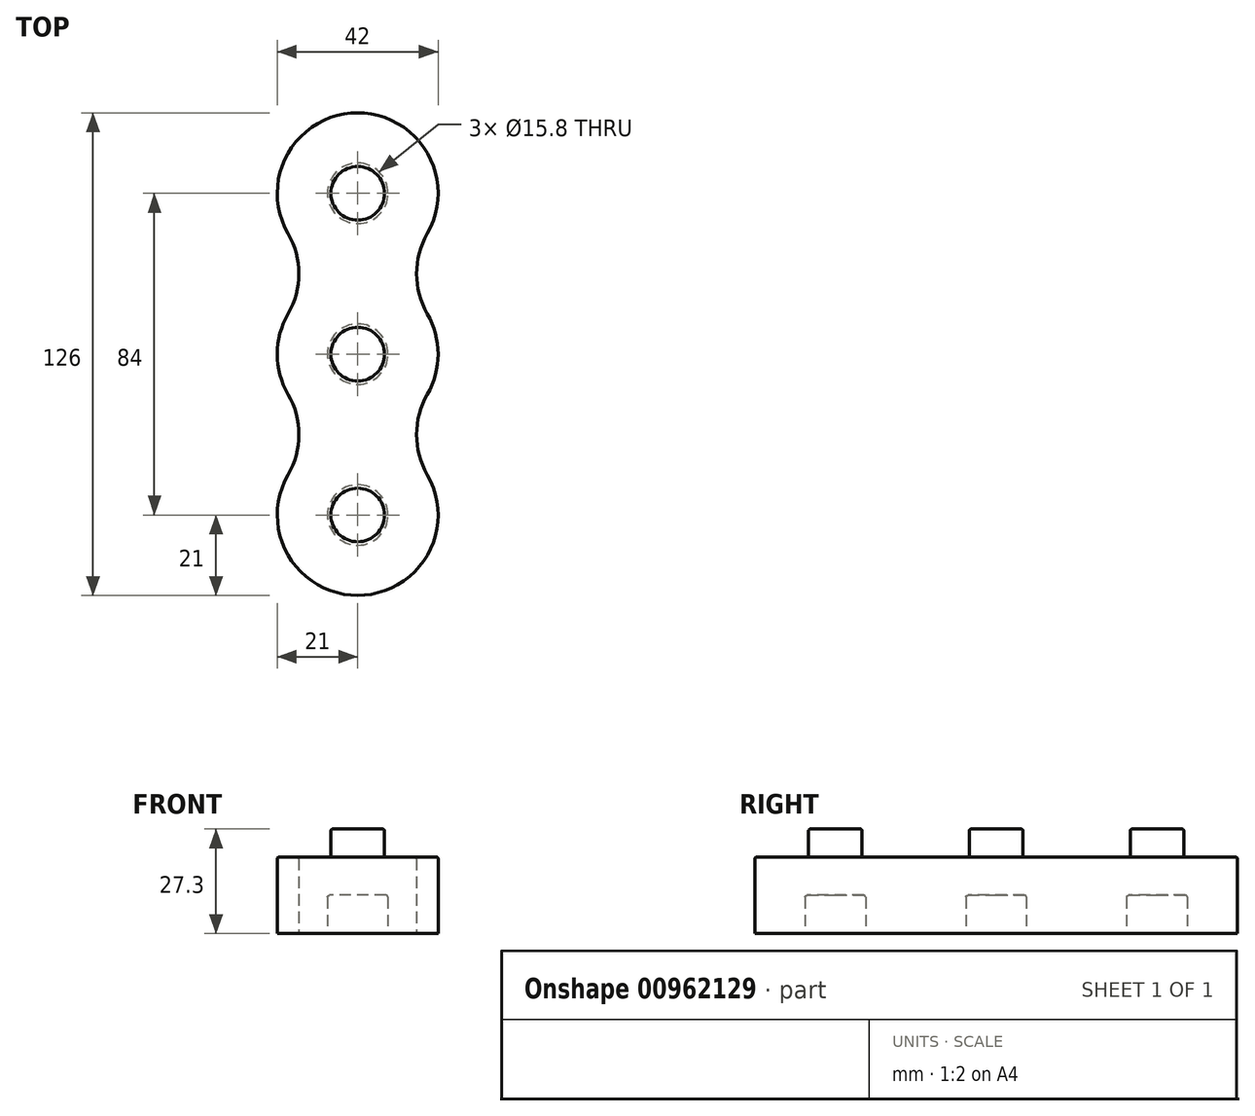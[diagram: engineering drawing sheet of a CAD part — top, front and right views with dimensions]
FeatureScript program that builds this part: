
annotation { "Feature Type Name" : "Feature", "Feature Type Description" : "" }
export const myFeature = defineFeature(function(context is Context, id is Id, definition is map)
    precondition{}
    {
        {
            assignVariable(context, id + "F0", {"name" : "inner_circle_extrude", "anyValue" : 10});
        }
        {
            assignVariable(context, id + "F1", {"name" : "nipple_circle_extrude", "anyValue" : 7.3});
        }
        {
            assignVariable(context, id + "F2", {"name" : "outer_circle_extrude", "anyValue" : 20});
        }
        {
            assignVariable(context, id + "F3", {"name" : "fillet", "anyValue" : 0.5});
        }
        {
            var Q0;
            Q0=qCreatedBy(makeId("Top.planeOp"),FACE);
            var sketch = newSketch(context, id + "F4", { "sketchPlane" : qUnion([Q0])});
            skCircle(sketch, "E0", {"center": v(0, 42) * mm, "radius": 7.9 * mm});
            skCircle(sketch, "E1", {"center": v(0, 0) * mm, "radius": 7.9 * mm});
            skArc(sketch, "E2.converted", {"start": v(18.19, 31.5) * mm, "mid": v(21, 42) * mm, "end": v(18.19, 52.5) * mm});
            skArc(sketch, "E3.converted", {"start": v(-18.19, 10.5) * mm, "mid": v(0, -21) * mm, "end": v(18.19, 10.5) * mm});
            skPoint(sketch, "E4.orphan", {"position": v(-18.87, 9.22) * mm});
            skArc(sketch, "E5", {"start": v(-18.19, 10.5) * mm, "mid": v(-15.37, 21) * mm, "end": v(-18.19, 31.5) * mm});
            skArc(sketch, "E6.MirrorC", {"start": v(18.19, 10.5) * mm, "mid": v(15.37, 21) * mm, "end": v(18.19, 31.5) * mm});
            skArc(sketch, "E7", {"start": v(18.19, 73.5) * mm, "mid": v(0, 105) * mm, "end": v(-18.19, 73.5) * mm});
            skArc(sketch, "E8", {"start": v(-18.19, 52.5) * mm, "mid": v(-15.37, 63) * mm, "end": v(-18.19, 73.5) * mm});
            skArc(sketch, "E9", {"start": v(18.19, 73.5) * mm, "mid": v(15.37, 63) * mm, "end": v(18.19, 52.5) * mm});
            skCircle(sketch, "E10", {"center": v(0, 84) * mm, "radius": 7.9 * mm});
            skArc(sketch, "E11.trimOffspring", {"start": v(-18.19, 52.5) * mm, "mid": v(-21, 42) * mm, "end": v(-18.19, 31.5) * mm});
            skSolve(sketch);
        }
        {
            var Q0;
            Q0=makeQuery(id+"F4.imprint","IMPRINT",FACE,{"disambiguationData":[TD([[makeQuery(id+"F4.imprint","IMPRINT",EDGE,{"derivedFrom":sQuery(id+"F4.wireOp",EDGE,"ScaTM9CG-l0WX-AUfX-dH3G-diZ5i2Zft3Bz")}),1.0]])]});
            var Q1;
            Q1=makeQuery(id+"F4.imprint","IMPRINT",FACE,{"disambiguationData":[TD([[makeQuery(id+"F4.imprint","IMPRINT",EDGE,{"derivedFrom":sQuery(id+"F4.wireOp",EDGE,"E0")}),1.0]])]});
            var Q2;
            Q2=makeQuery(id+"F4.imprint","IMPRINT",FACE,{"disambiguationData":[TD([[makeQuery(id+"F4.imprint","IMPRINT",EDGE,{"derivedFrom":sQuery(id+"F4.wireOp",EDGE,"E1")}),1.0]])]});
            var Q3;
            Q3=makeQuery(id+"F4.imprint","IMPRINT",FACE,{"disambiguationData":[TD([[makeQuery(id+"F4.imprint","IMPRINT",EDGE,{"derivedFrom":sQuery(id+"F4.wireOp",EDGE,"E0")}),-1.0]])]});
            var Q4;
            Q4=makeQuery(id+"F4.imprint","IMPRINT",FACE,{"disambiguationData":[TD([[makeQuery(id+"F4.imprint","IMPRINT",EDGE,{"derivedFrom":sQuery(id+"F4.wireOp",EDGE,"E10")}),1.0]])]});
            extrude(context, id + "F5", {"entities" : qUnion([Q0, Q1, Q2, Q3, Q4]), "depth" : (getVariable(context, 'outer_circle_extrude')) * mm, "offsetDistance" : 25 * mm});
        }
        {
            var Q0;
            Q0=makeQuery(id+"F4.imprint","IMPRINT",FACE,{"disambiguationData":[TD([[makeQuery(id+"F4.imprint","IMPRINT",EDGE,{"derivedFrom":sQuery(id+"F4.wireOp",EDGE,"E0")}),1.0]])]});
            var Q1;
            Q1=makeQuery(id+"F4.imprint","IMPRINT",FACE,{"disambiguationData":[TD([[makeQuery(id+"F4.imprint","IMPRINT",EDGE,{"derivedFrom":sQuery(id+"F4.wireOp",EDGE,"E1")}),1.0]])]});
            var Q2;
            Q2=makeQuery(id+"F4.imprint","IMPRINT",FACE,{"disambiguationData":[TD([[makeQuery(id+"F4.imprint","IMPRINT",EDGE,{"derivedFrom":sQuery(id+"F4.wireOp",EDGE,"E10")}),1.0]])]});
            extrude(context, id + "F6", {"entities" : qUnion([Q0, Q1, Q2]), "operationType" : NewBodyOperationType.REMOVE, "depth" : (getVariable(context, 'inner_circle_extrude')) * mm, "offsetDistance" : 25 * mm});
        }
        {
            var Q0;
            Q0=makeQuery(id+"F5.opExtrude","CAP_FACE",FACE,{"disambiguationData":[OSD([sQuery(id+"F4.wireOp",EDGE,"E2.converted"),sQuery(id+"F4.wireOp",EDGE,"E3.converted"),sQuery(id+"F4.wireOp",EDGE,"E5"),sQuery(id+"F4.wireOp",EDGE,"E6.MirrorC")])],"isStart":false});
            var sketch = newSketch(context, id + "F7", { "sketchPlane" : qUnion([Q0])});
            skCircle(sketch, "E12", {"center": v(0, 0) * mm, "radius": 7 * mm});
            skCircle(sketch, "E13", {"center": v(0, 42) * mm, "radius": 7 * mm});
            skCircle(sketch, "E14", {"center": v(0, 84) * mm, "radius": 7 * mm});
            skSolve(sketch);
        }
        {
            var Q0;
            Q0=makeQuery(id+"F7.imprint","IMPRINT",FACE,{"disambiguationData":[TD([[makeQuery(id+"F7.imprint","IMPRINT",EDGE,{"derivedFrom":sQuery(id+"F7.wireOp",EDGE,"E12")}),1.0]])]});
            var Q1;
            Q1=makeQuery(id+"F7.imprint","IMPRINT",FACE,{"disambiguationData":[TD([[makeQuery(id+"F7.imprint","IMPRINT",EDGE,{"derivedFrom":sQuery(id+"F7.wireOp",EDGE,"Dg55u7MG-Wcnn-qXMQ-j3jR-78wnB7IFwmOc")}),1.0]])]});
            var Q2;
            Q2=makeQuery(id+"F7.imprint","IMPRINT",FACE,{"disambiguationData":[TD([[makeQuery(id+"F7.imprint","IMPRINT",EDGE,{"derivedFrom":sQuery(id+"F7.wireOp",EDGE,"E13")}),1.0]])]});
            var Q3;
            Q3=makeQuery(id+"F7.imprint","IMPRINT",FACE,{"disambiguationData":[TD([[makeQuery(id+"F7.imprint","IMPRINT",EDGE,{"derivedFrom":sQuery(id+"F7.wireOp",EDGE,"E14")}),1.0]])]});
            extrude(context, id + "F8", {"entities" : qUnion([Q0, Q1, Q2, Q3]), "operationType" : NewBodyOperationType.ADD, "depth" : (getVariable(context, 'nipple_circle_extrude')) * mm, "offsetDistance" : 25 * mm});
        }
        {
            var Q0;
            Q0=makeQuery(id+"F8.opExtrude","CAP_EDGE",EDGE,{"disambiguationData":[OSD([sQuery(id+"F7.wireOp",EDGE,"E12")])],"isStart":false});
            var Q1;
            Q1=makeQuery(id+"F5.opExtrude","CAP_EDGE",EDGE,{"disambiguationData":[OSD([sQuery(id+"F4.wireOp",EDGE,"ScaTM9CG-l0WX-AUfX-dH3G-diZ5i2Zft3Bz")])],"isStart":false});
            var Q2;
            Q2=makeQuery(id+"F5.opExtrude","CAP_EDGE",EDGE,{"disambiguationData":[OSD([sQuery(id+"F4.wireOp",EDGE,"ScaTM9CG-l0WX-AUfX-dH3G-diZ5i2Zft3Bz")])],"isStart":true});
            var Q3;
            Q3=makeQuery(id+"F6.boolean.opBoolean","COPY",EDGE,{"derivedFrom":makeQuery(id+"F6.opExtrude","CAP_EDGE",EDGE,{"disambiguationData":[OSD([sQuery(id+"F4.wireOp",EDGE,"E0")])],"isStart":true})});
            var Q4;
            Q4=makeQuery(id+"F6.boolean.opBoolean","COPY",FACE,{"derivedFrom":makeQuery(id+"F6.opExtrude","CAP_FACE",FACE,{"disambiguationData":[OSD([sQuery(id+"F4.wireOp",EDGE,"E0")])],"isStart":false})});
            var Q5;
            Q5=makeQuery(id+"F6.boolean.opBoolean","COPY",EDGE,{"derivedFrom":makeQuery(id+"F6.opExtrude","CAP_EDGE",EDGE,{"disambiguationData":[OSD([sQuery(id+"F4.wireOp",EDGE,"E1")])],"isStart":true})});
            var Q6;
            Q6=makeQuery(id+"F6.boolean.opBoolean","COPY",EDGE,{"derivedFrom":makeQuery(id+"F6.opExtrude","CAP_EDGE",EDGE,{"disambiguationData":[OSD([sQuery(id+"F4.wireOp",EDGE,"E1")])],"isStart":false})});
            var Q7;
            Q7=makeQuery(id+"F8.opExtrude","CAP_EDGE",EDGE,{"disambiguationData":[OSD([sQuery(id+"F7.wireOp",EDGE,"Dg55u7MG-Wcnn-qXMQ-j3jR-78wnB7IFwmOc")])],"isStart":true});
            var Q8;
            Q8=makeQuery(id+"F8.opExtrude","CAP_EDGE",EDGE,{"disambiguationData":[OSD([sQuery(id+"F7.wireOp",EDGE,"Dg55u7MG-Wcnn-qXMQ-j3jR-78wnB7IFwmOc")])],"isStart":false});
            var Q9;
            Q9=makeQuery(id+"F8.opExtrude","CAP_EDGE",EDGE,{"disambiguationData":[OSD([sQuery(id+"F7.wireOp",EDGE,"E13")])],"isStart":false});
            var Q10;
            Q10=makeQuery(id+"F8.opExtrude","CAP_EDGE",EDGE,{"disambiguationData":[OSD([sQuery(id+"F7.wireOp",EDGE,"E13")])],"isStart":true});
            var Q11;
            Q11=makeQuery(id+"F5.opExtrude","CAP_EDGE",EDGE,{"disambiguationData":[OSD([sQuery(id+"F4.wireOp",EDGE,"E2.converted")])],"isStart":false});
            var Q12;
            Q12=makeQuery(id+"F8.opExtrude","CAP_EDGE",EDGE,{"disambiguationData":[OSD([sQuery(id+"F7.wireOp",EDGE,"E14")])],"isStart":false});
            var Q13;
            Q13=makeQuery(id+"F8.opExtrude","CAP_EDGE",EDGE,{"disambiguationData":[OSD([sQuery(id+"F7.wireOp",EDGE,"E14")])],"isStart":true});
            var Q14;
            Q14=makeQuery(id+"F6.boolean.opBoolean","COPY",EDGE,{"derivedFrom":makeQuery(id+"F6.opExtrude","CAP_EDGE",EDGE,{"disambiguationData":[OSD([sQuery(id+"F4.wireOp",EDGE,"E10")])],"isStart":false})});
            var Q15;
            Q15=makeQuery(id+"F6.boolean.opBoolean","COPY",EDGE,{"derivedFrom":makeQuery(id+"F6.opExtrude","CAP_EDGE",EDGE,{"disambiguationData":[OSD([sQuery(id+"F4.wireOp",EDGE,"E10")])],"isStart":true})});
            var Q16;
            Q16=makeQuery(id+"F8.opExtrude","CAP_EDGE",EDGE,{"disambiguationData":[OSD([sQuery(id+"F7.wireOp",EDGE,"E12")])],"isStart":true});
            fillet(context, id + "F9", {"entities" : qUnion([Q0, Q1, Q2, Q3, Q4, Q5, Q6, Q7, Q8, Q9, Q10, Q11, Q12, Q13, Q14, Q15, Q16]), "radius" : (getVariable(context, 'fillet')) * mm, "tangentPropagation" : true, "allowEdgeOverflow" : false});
        }
    });
